# Revit family: CFS4 (6RED+2RJ45)
name_source: partatom
category: Aparatos eléctricos
revit_build: Autodesk Revit 2017 (Build: 20171027_0315(x64)
units: mm (PartAtom-declared; Revit-internal decimal feet)

## family parameters
Anfitrión = Cara
Compartido = No
Corte con vacíos al cargar = No
Cota de conector redondo = Diámetro de uso
Mantener orientación de anotación = No
Número OmniClass = 23.80.50.11.11
Punto de cálculo de habitación = No
Tipo de pieza = Normal
Título OmniClass = Receptacle Terminal Units

## types (1)
- Gama Plus
    Acabado caja = Gris RAL7011 / Grafico RAL7021
    Acabado marco = Blanco nieve RAL9010
    CFS47-CF49 (AltoxLargoxAncho) = 70-90x295x158 mm
    Capacidad = 3-4 módulos Standard / 6 tomas de corriente eléctrica y 2 tomas RJ45
    Carga eléctrica = Potencia
    Compatibilidad = Gama PLUS
    Composición = Cubeta, Marco, Tornillería marco (4ud), Anclajes (4ud), Separador, Pasacables (2ud), Toma de tierra, Tapa metálica, Tornillos de regulación, Espacio para 2 conectores CR
    Código de montaje = D5020100
    Descripción = Caja de conexiones empotrable CFS4 con 6 tomas de corriente y 2 tomas de red RJ45
    Elevación por defecto = 1200 mm
    Fabricante = MMCONECTA
    Factor de potencia = 1
    Instalación = Empotrado en suelo técnico / pavimento
    Materia prima = Policarbonato libre de halógenos
    Modelo = CFS4
    Normativas = UNE 60670 / Marcado CE / IK08
    Polos = 1
    Potencia aparente = 3500 W
    URL = http://www.mmconecta.com
    Voltaje = 230 V

## geometry (parser evidence)
native form markers: Blend x4
no freeform markers — native parametric forms only
